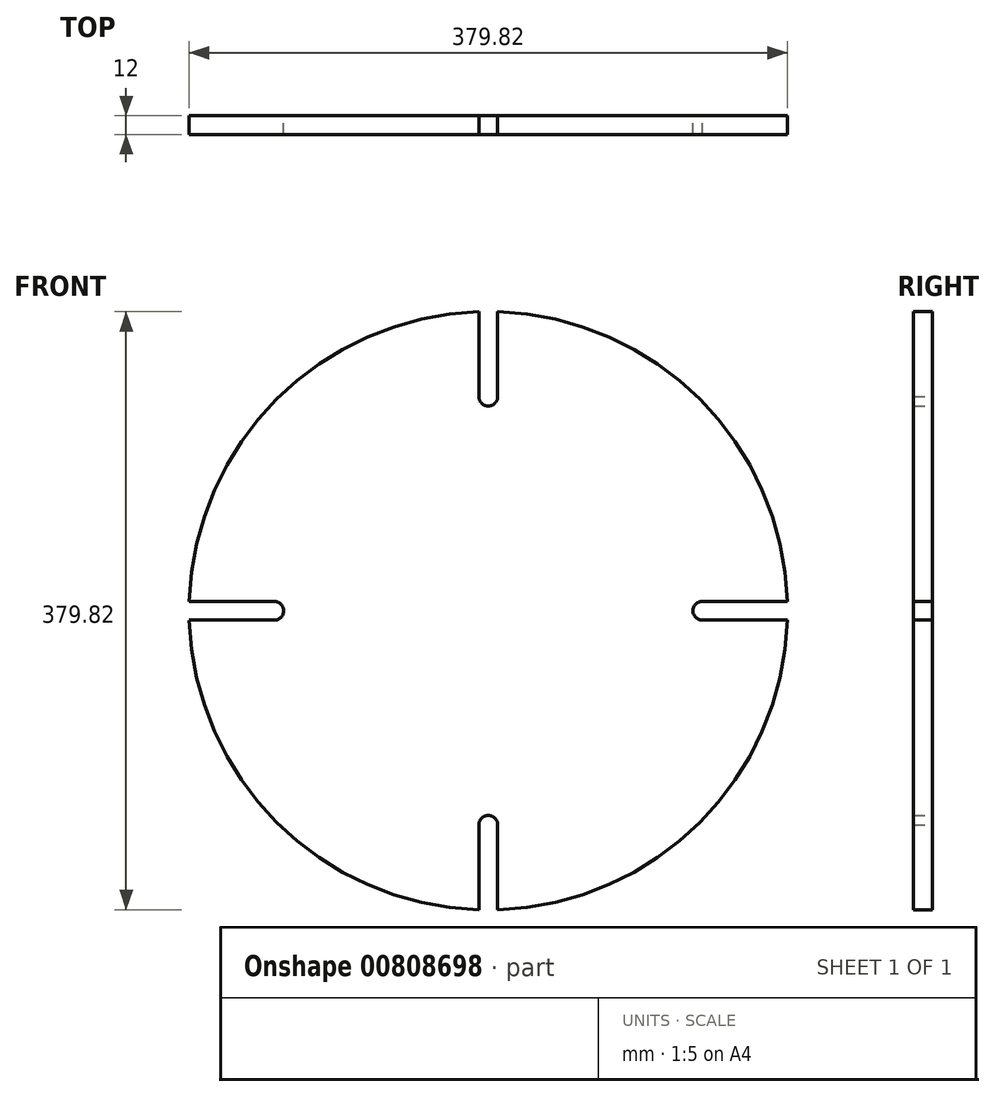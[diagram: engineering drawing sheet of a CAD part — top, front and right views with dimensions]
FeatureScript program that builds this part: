
annotation { "Feature Type Name" : "Feature", "Feature Type Description" : "" }
export const myFeature = defineFeature(function(context is Context, id is Id, definition is map)
    precondition{}
    {
        {
            var Q0;
            Q0=qCreatedBy(makeId("Front.planeOp"),FACE);
            var sketch = newSketch(context, id + "F0", { "sketchPlane" : qUnion([Q0])});
            skArc(sketch, "E0", {"start": v(-6, 189.9) * mm, "mid": v(-134.35, 134.35) * mm, "end": v(-189.9, 6) * mm});
            skArc(sketch, "E1", {"start": v(-6, 136.13) * mm, "mid": v(0, 130) * mm, "end": v(6, 136.13) * mm});
            skArc(sketch, "E2", {"start": v(135.87, 6) * mm, "mid": v(130, -0.13) * mm, "end": v(136.13, -6) * mm});
            skArc(sketch, "E3", {"start": v(6, -136.13) * mm, "mid": v(0, -130) * mm, "end": v(-6, -136.13) * mm});
            skArc(sketch, "E4", {"start": v(-136, -6) * mm, "mid": v(-130, 0) * mm, "end": v(-136, 6) * mm});
            skLineSegment(sketch, "E5", {"start": v(6, 135.87) * mm, "end": v(6, 189.9) * mm});
            skLineSegment(sketch, "E6", {"start": v(-6, 135.87) * mm, "end": v(-6, 189.9) * mm});
            skLineSegment(sketch, "E7", {"start": v(135.87, 6) * mm, "end": v(189.9, 6) * mm});
            skLineSegment(sketch, "E8", {"start": v(135.87, -6) * mm, "end": v(189.9, -6) * mm});
            skArc(sketch, "E9.trimOffspring", {"start": v(189.9, 6) * mm, "mid": v(134.35, 134.35) * mm, "end": v(6, 189.9) * mm});
            skLineSegment(sketch, "E10", {"start": v(-6, -135.87) * mm, "end": v(-6, -189.9) * mm});
            skLineSegment(sketch, "E11", {"start": v(6, -135.87) * mm, "end": v(6, -189.9) * mm});
            skArc(sketch, "E12.trimOffspring", {"start": v(6, -189.9) * mm, "mid": v(134.35, -134.35) * mm, "end": v(189.9, -6) * mm});
            skLineSegment(sketch, "E13", {"start": v(-136, 6) * mm, "end": v(-189.9, 6) * mm});
            skLineSegment(sketch, "E14", {"start": v(-136, -6) * mm, "end": v(-189.9, -6) * mm});
            skArc(sketch, "E15.trimOffspring", {"start": v(-189.9, -6) * mm, "mid": v(-134.35, -134.35) * mm, "end": v(-6, -189.9) * mm});
            skSolve(sketch);
        }
        {
            var Q0;
            {var subQ12=sQuery(id+"F0.wireOp",EDGE,"E0");Q0=makeQuery(id+"F0.imprint","IMPRINT",FACE,{"disambiguationData":[TD([[makeQuery(id+"F0.imprint","IMPRINT",EDGE,{"derivedFrom":subQ12}),1.0]])]});}
            extrude(context, id + "F1", {"entities" : qUnion([Q0]), "depth" : 12 * mm, "offsetDistance" : 25 * mm});
        }
    });
